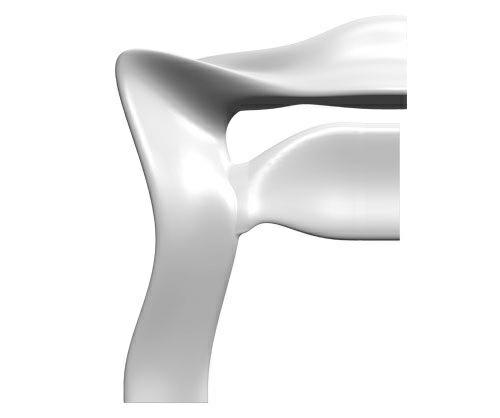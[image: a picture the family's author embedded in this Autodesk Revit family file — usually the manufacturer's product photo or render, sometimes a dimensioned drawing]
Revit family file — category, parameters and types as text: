
# Revit family: CITY ALPHABET litera „F”
name_source: partatom
category: Meble
revit_build: Autodesk Revit 2018 (Build: 20190510_1515(x64)
units: mm (PartAtom-declared; Revit-internal decimal feet)

## family parameters
Numer OmniClass = 23.40.10.11.14
Obiekt nadrzędny = Powierzchnia
Punkt obliczania pomieszczeń = Nie
Tnij formami wycięć po wczytaniu = Nie
Tytuł OmniClass = Exterior Seating
Współdzielony = Nie

## types (1)
- CITY ALPHABET litera „F”
    Domyślna rzędna = 1219 mm
    Długość = 2190 mm  [stored 7.18504 ft]
    IfcExportAs = IfcFurnishingElement
    Komentarze do typu = Ławka
    Materiał - informacja = Szeroki wybór kolorów wg palety RAL. Istnieje również możliwość specjalnego wykonania
kolorystycznego na indywidualne zapytanie klienta.
    Model = CITY ALPHABET litera „F”
    Obraz typu = F.jpg
    Producent = Astrini Design
    Szerokość = 1650 mm  [stored 5.41339 ft]
    Temepratura użytkowania = -40°C do 80°C, ( -40°F do 176°F )
    URL = http://astrini-design.pl
    Waga (szacunkowo) = 62.00 kg
    Waga po wypełnieniu (szacunkowo) = 112.00 kg
    Wysokość = 1100 mm

note: [stored X ft] marks values corroborated as IEEE doubles in the binary element streams (Revit-internal decimal feet)
